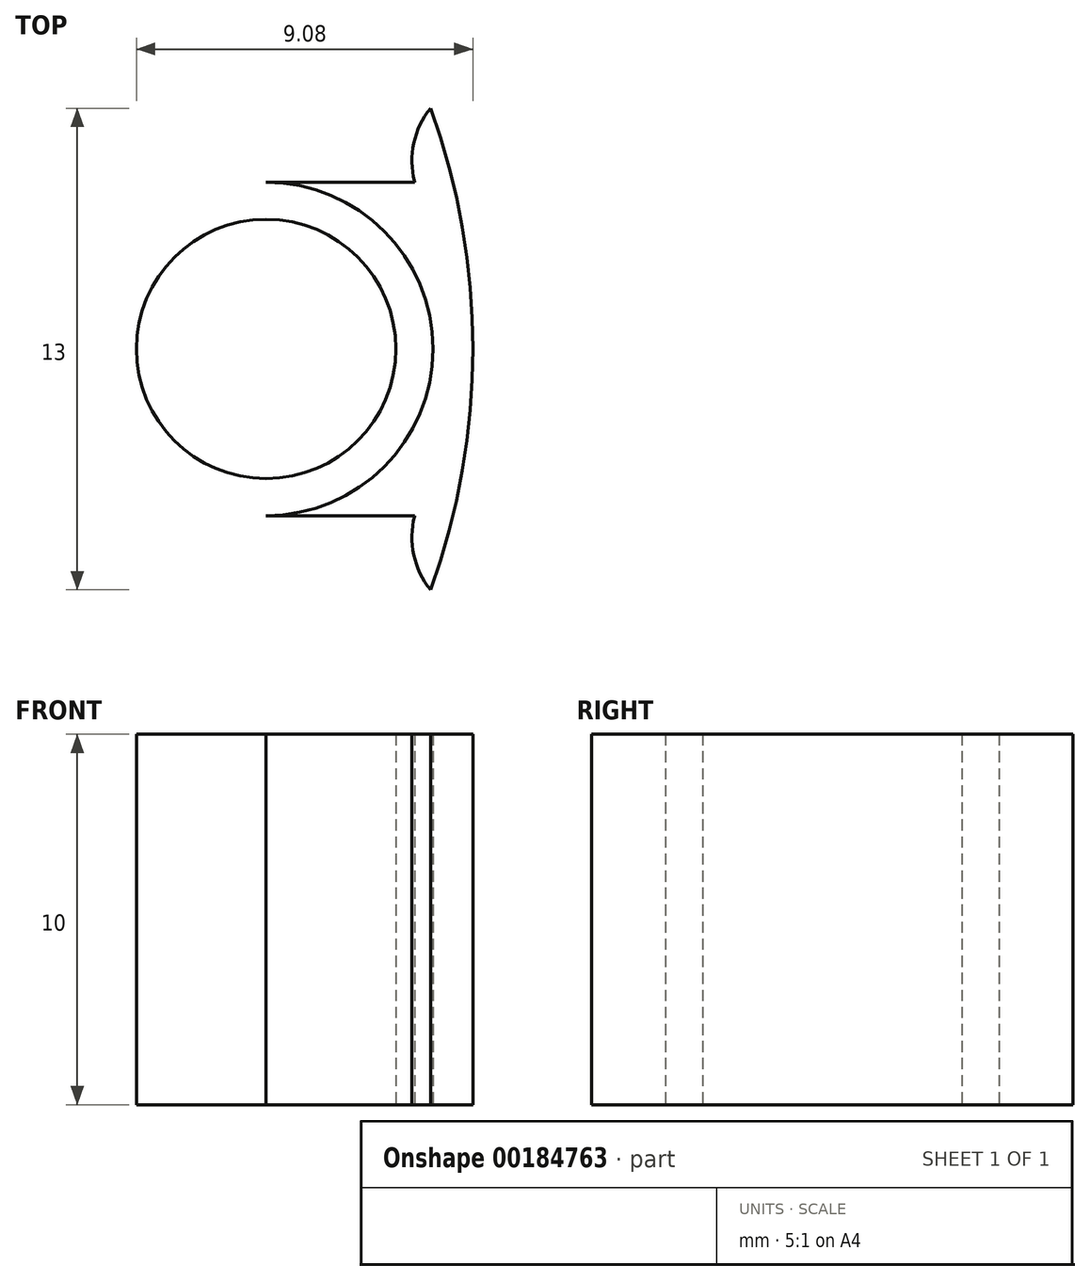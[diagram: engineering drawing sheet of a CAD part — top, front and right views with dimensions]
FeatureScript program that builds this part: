
annotation { "Feature Type Name" : "Feature", "Feature Type Description" : "" }
export const myFeature = defineFeature(function(context is Context, id is Id, definition is map)
    precondition{}
    {
        {
            var Q0;
            Q0=qCreatedBy(makeId("Top.planeOp"),FACE);
            var sketch = newSketch(context, id + "F0", { "sketchPlane" : qUnion([Q0])});
            skCircle(sketch, "E0", {"center": v(0, 0) * mm, "radius": 19 * mm});
            skLineSegment(sketch, "E1", {"start": v(0, 0) * mm, "end": v(17.85, -6.5) * mm});
            skLineSegment(sketch, "E2", {"start": v(0, 0) * mm, "end": v(17.85, 6.5) * mm});
            skCircle(sketch, "E3", {"center": v(0, 0) * mm, "radius": 18 * mm});
            skPoint(sketch, "E4", {"position": v(16.91, -6.16) * mm});
            skPoint(sketch, "E5", {"position": v(16.91, 6.16) * mm});
            skLineSegment(sketch, "E6", {"start": v(18.46, 12.24) * mm, "end": v(18.46, -20.23) * mm, "construction": true});
            skCircle(sketch, "E7.MirrorC", {"center": v(13.42, 0) * mm, "radius": 4.5 * mm});
            skCircle(sketch, "E8.MirrorC", {"center": v(13.42, 0) * mm, "radius": 3.5 * mm});
            skLineSegment(sketch, "E9.MirrorCS", {"start": v(13.42, 4.5) * mm, "end": v(18.46, 4.5) * mm});
            skLineSegment(sketch, "E10.MirrorCS", {"start": v(13.42, -4.5) * mm, "end": v(18.46, -4.5) * mm});
            skSolve(sketch);
        }
        {
            var Q0;
            {var subQ0=sQuery(id+"F0.wireOp",EDGE,"E2");var subQ1=sQuery(id+"F0.wireOp",EDGE,"E0");var subQ2=makeQuery(id+"F0.imprint","INTERSECT",VERTEX,{"derivedFrom":[subQ1,subQ0]});Q0=makeQuery(id+"F0.imprint","IMPRINT",FACE,{"disambiguationData":[TD([[makeQuery(id+"F0.imprint","IMPRINT",EDGE,{"disambiguationData":[TD([[subQ2,1.0]])],"derivedFrom":subQ1}),1.0]])]});}
            var Q1;
            {var subQ0=sQuery(id+"F0.wireOp",EDGE,"E1");var subQ1=sQuery(id+"F0.wireOp",EDGE,"E0");var subQ2=makeQuery(id+"F0.imprint","INTERSECT",VERTEX,{"derivedFrom":[subQ1,subQ0]});Q1=makeQuery(id+"F0.imprint","IMPRINT",FACE,{"disambiguationData":[TD([[makeQuery(id+"F0.imprint","IMPRINT",EDGE,{"disambiguationData":[TD([[subQ2,-1.0]])],"derivedFrom":subQ1}),1.0]])]});}
            var Q2;
            {var subQ0=sQuery(id+"F0.wireOp",EDGE,"E9.MirrorCS");var subQ1=sQuery(id+"F0.wireOp",EDGE,"E0");var subQ2=makeQuery(id+"F0.imprint","INTERSECT",VERTEX,{"derivedFrom":[subQ1,subQ0]});Q2=makeQuery(id+"F0.imprint","IMPRINT",FACE,{"disambiguationData":[TD([[makeQuery(id+"F0.imprint","IMPRINT",EDGE,{"disambiguationData":[TD([[subQ2,1.0]])],"derivedFrom":subQ1}),1.0]])]});}
            var Q3;
            {var subQ0=sQuery(id+"F0.wireOp",EDGE,"E9.MirrorCS");var subQ1=sQuery(id+"F0.wireOp",EDGE,"E3");var subQ2=makeQuery(id+"F0.imprint","INTERSECT",VERTEX,{"derivedFrom":[subQ1,subQ0]});Q3=makeQuery(id+"F0.imprint","IMPRINT",FACE,{"disambiguationData":[TD([[makeQuery(id+"F0.imprint","IMPRINT",EDGE,{"disambiguationData":[TD([[subQ2,1.0]])],"derivedFrom":subQ1}),1.0]])]});}
            var Q4;
            Q4=makeQuery(id+"F0.imprint","IMPRINT",FACE,{"disambiguationData":[TD([[makeQuery(id+"F0.imprint","IMPRINT",EDGE,{"derivedFrom":sQuery(id+"F0.wireOp",EDGE,"E8.MirrorC")}),1.0]])]});
            extrude(context, id + "F1", {"entities" : qUnion([Q0, Q1, Q2, Q3, Q4]), "depth" : 10 * mm});
        }
        {
            var Q0;
            Q0=makeQuery(id+"F1.opExtrude","SWEPT_EDGE",EDGE,{"disambiguationData":[OSD([sQuery(id+"F0.wireOp",EDGE,"E1"),sQuery(id+"F0.wireOp",EDGE,"E3")])]});
            var Q1;
            Q1=makeQuery(id+"F1.opExtrude","SWEPT_EDGE",EDGE,{"disambiguationData":[OSD([sQuery(id+"F0.wireOp",EDGE,"E2"),sQuery(id+"F0.wireOp",EDGE,"E3")])]});
            fillet(context, id + "F2", {"entities" : qUnion([Q0, Q1]), "radius" : 2.25 * mm, "tangentPropagation" : true, "allowEdgeOverflow" : false});
        }
    });
